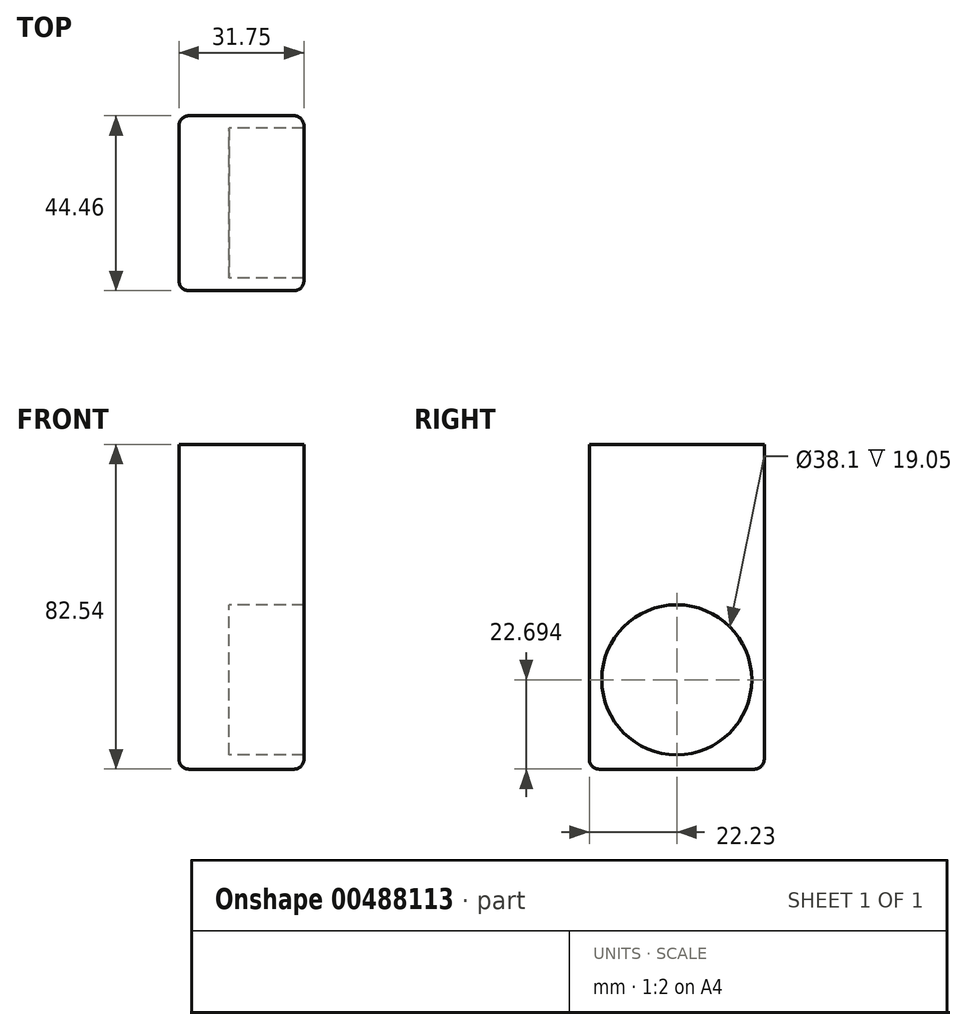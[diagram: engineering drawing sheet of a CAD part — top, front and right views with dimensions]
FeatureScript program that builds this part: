
annotation { "Feature Type Name" : "Feature", "Feature Type Description" : "" }
export const myFeature = defineFeature(function(context is Context, id is Id, definition is map)
    precondition{}
    {
        {
            var Q0;
            Q0=qCreatedBy(makeId("Right.planeOp"),FACE);
            var sketch = newSketch(context, id + "F0", { "sketchPlane" : qUnion([Q0])});
            skLineSegment(sketch, "E0.bottom", {"start": v(22.23, 41.28) * mm, "end": v(-22.23, 41.28) * mm});
            skLineSegment(sketch, "E0.top", {"start": v(22.22, -41.28) * mm, "end": v(-22.23, -41.28) * mm});
            skLineSegment(sketch, "E0.left", {"start": v(22.23, 41.28) * mm, "end": v(22.22, -41.28) * mm});
            skLineSegment(sketch, "E0.right", {"start": v(-22.23, 41.28) * mm, "end": v(-22.23, -41.28) * mm});
            skPoint(sketch, "E0.middle", {"position": v(0, 0) * mm});
            skCircle(sketch, "E1", {"center": v(0, -18.58) * mm, "radius": 19.05 * mm});
            skSolve(sketch);
        }
        {
            var Q0;
            Q0=makeQuery(id+"F0.imprint","IMPRINT",FACE,{"disambiguationData":[TD([[makeQuery(id+"F0.imprint","IMPRINT",EDGE,{"derivedFrom":sQuery(id+"F0.wireOp",EDGE,"E1")}),1.0]])]});
            extrude(context, id + "F1", {"entities" : qUnion([Q0]), "depth" : 12.7 * mm});
        }
        {
            var Q0;
            Q0=makeQuery(id+"F0.imprint","IMPRINT",FACE,{"disambiguationData":[TD([[makeQuery(id+"F0.imprint","IMPRINT",EDGE,{"derivedFrom":sQuery(id+"F0.wireOp",EDGE,"E0.bottom")}),1.0]])]});
            extrude(context, id + "F2", {"entities" : qUnion([Q0]), "operationType" : NewBodyOperationType.ADD, "depth" : 31.75 * mm});
        }
        {
            var Q0;
            Q0=makeQuery(id+"F2.opExtrude","SWEPT_EDGE",EDGE,{"disambiguationData":[OSD([sQuery(id+"F0.wireOp",EDGE,"E0.top"),sQuery(id+"F0.wireOp",EDGE,"E0.right")])]});
            var Q1;
            Q1=makeQuery(id+"F2.opExtrude","SWEPT_EDGE",EDGE,{"disambiguationData":[OSD([sQuery(id+"F0.wireOp",EDGE,"E0.top"),sQuery(id+"F0.wireOp",EDGE,"E0.left")])]});
            var Q2;
            Q2=makeQuery(id+"F2.opExtrude","CAP_EDGE",EDGE,{"disambiguationData":[OSD([sQuery(id+"F0.wireOp",EDGE,"E0.top")])],"isStart":true});
            var Q3;
            Q3=makeQuery(id+"F2.opExtrude","CAP_EDGE",EDGE,{"disambiguationData":[OSD([sQuery(id+"F0.wireOp",EDGE,"E0.top")])],"isStart":false});
            var Q4;
            Q4=makeQuery(id+"F2.opExtrude","CAP_EDGE",EDGE,{"disambiguationData":[OSD([sQuery(id+"F0.wireOp",EDGE,"E0.left")])],"isStart":false});
            var Q5;
            Q5=makeQuery(id+"F2.opExtrude","CAP_EDGE",EDGE,{"disambiguationData":[OSD([sQuery(id+"F0.wireOp",EDGE,"E0.left")])],"isStart":true});
            var Q6;
            Q6=makeQuery(id+"F2.opExtrude","CAP_EDGE",EDGE,{"disambiguationData":[OSD([sQuery(id+"F0.wireOp",EDGE,"E0.right")])],"isStart":true});
            var Q7;
            Q7=makeQuery(id+"F2.opExtrude","CAP_EDGE",EDGE,{"disambiguationData":[OSD([sQuery(id+"F0.wireOp",EDGE,"E0.right")])],"isStart":false});
            fillet(context, id + "F3", {"entities" : qUnion([Q0, Q1, Q2, Q3, Q4, Q5, Q6, Q7]), "radius" : 2.54 * mm, "tangentPropagation" : true, "allowEdgeOverflow" : false});
        }
    });
